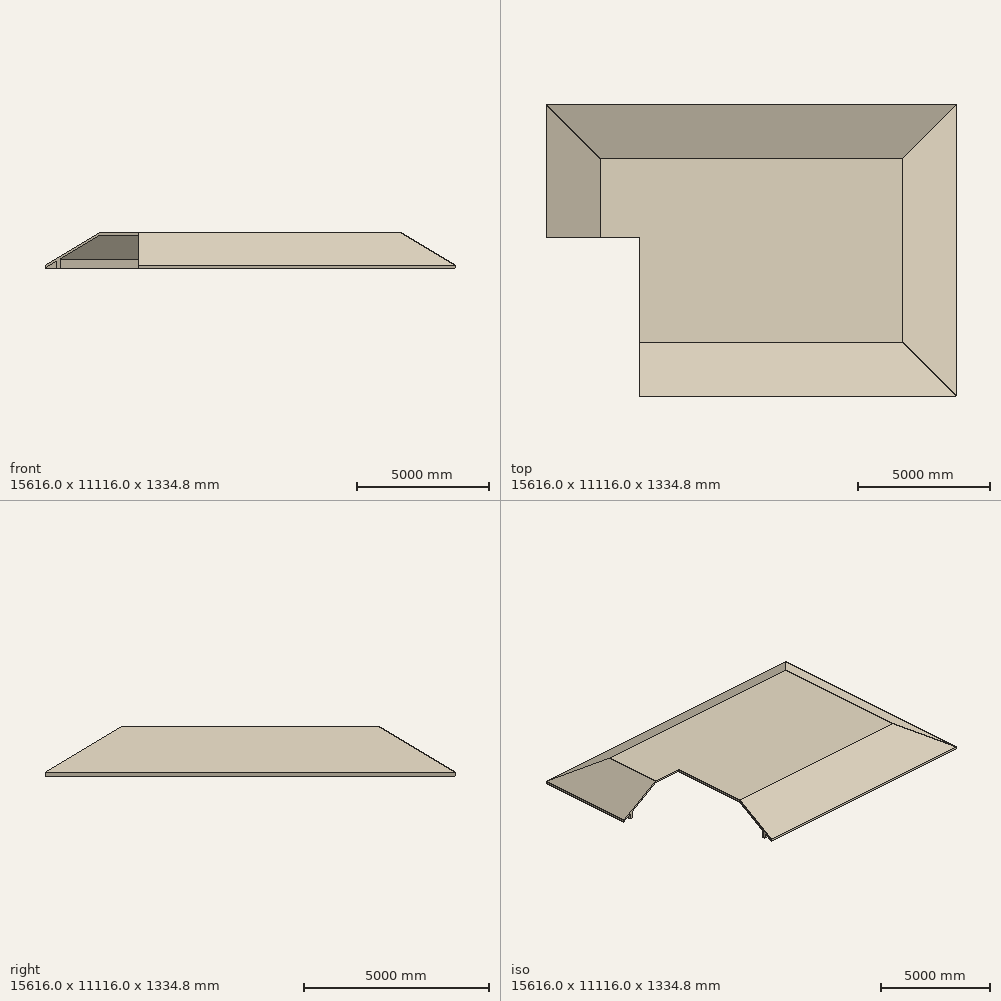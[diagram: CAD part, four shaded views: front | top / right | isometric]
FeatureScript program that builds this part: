
annotation { "Feature Type Name" : "Feature", "Feature Type Description" : "" }
export const myFeature = defineFeature(function(context is Context, id is Id, definition is map)
    precondition{}
    {
        {
            var Q0;
            Q0=qCreatedBy(makeId("Front.planeOp"),FACE);
            var sketch = newSketch(context, id + "F0", { "sketchPlane" : qUnion([Q0])});
            skLineSegment(sketch, "E0", {"start": v(1341.6, 842.92) * mm, "end": v(-158.4, -57.08) * mm});
            skLineSegment(sketch, "E1", {"start": v(-158.4, -57.08) * mm, "end": v(-158.4, -57.08) * mm});
            skLineSegment(sketch, "E2", {"start": v(-716.39, -391.87) * mm, "end": v(-716.39, -291.87) * mm});
            skLineSegment(sketch, "E3", {"start": v(-716.39, -291.87) * mm, "end": v(1341.6, 942.92) * mm});
            skLineSegment(sketch, "E4", {"start": v(1341.6, 942.92) * mm, "end": v(1341.6, 842.92) * mm});
            skLineSegment(sketch, "E5.bottom", {"start": v(-158.4, -391.87) * mm, "end": v(-308.4, -391.87) * mm});
            skLineSegment(sketch, "E5.left", {"start": v(-158.4, -391.87) * mm, "end": v(-158.4, -57.08) * mm});
            skLineSegment(sketch, "E5.right", {"start": v(-308.4, -391.87) * mm, "end": v(-308.4, -147.08) * mm});
            skLineSegment(sketch, "E6.trimOffspring", {"start": v(-308.4, -147.08) * mm, "end": v(-716.39, -391.87) * mm});
            skSolve(sketch);
        }
        {
            var Q0;
            Q0 = qSketchRegion(id + "F0", true);
            var Q1;
            Q1 = qBodyType(qCreatedBy(id + "F0" ,EDGE), BodyType.WIRE);
            extrude(context, id + "F1", {"entities" : qUnion([Q0]), "surfaceEntities" : qUnion([Q1]), "oppositeDirection" : true, "depth" : 5058 * mm, "offsetDistance" : 25 * mm});
        }
        {
            var Q0;
            Q0=makeQuery(id+"F1.opExtrude","SWEPT_FACE",FACE,{"disambiguationData":[OSD([sQuery(id+"F0.wireOp",EDGE,"E2")])]});
            var sketch = newSketch(context, id + "F2", { "sketchPlane" : qUnion([Q0])});
            skLineSegment(sketch, "E7", {"start": v(-3000.02, 842.92) * mm, "end": v(-4500.02, -57.08) * mm});
            skLineSegment(sketch, "E8", {"start": v(-4500.02, -57.08) * mm, "end": v(-4500.02, -57.08) * mm});
            skLineSegment(sketch, "E9", {"start": v(-5058, -391.87) * mm, "end": v(-5058, -291.87) * mm});
            skLineSegment(sketch, "E10", {"start": v(-5058, -291.87) * mm, "end": v(-3000.02, 942.92) * mm});
            skLineSegment(sketch, "E11", {"start": v(-3000.02, 942.92) * mm, "end": v(-3000.02, 842.92) * mm});
            skLineSegment(sketch, "E12.bottom", {"start": v(-4500.02, -391.87) * mm, "end": v(-4650.02, -391.87) * mm});
            skLineSegment(sketch, "E12.left", {"start": v(-4500.02, -391.87) * mm, "end": v(-4500.02, -57.08) * mm});
            skLineSegment(sketch, "E12.right", {"start": v(-4650.02, -391.87) * mm, "end": v(-4650.02, -147.08) * mm});
            skLineSegment(sketch, "E13.trimOffspring", {"start": v(-4650.02, -147.08) * mm, "end": v(-5058, -391.87) * mm});
            skSolve(sketch);
        }
        {
            var Q0;
            Q0 = qSketchRegion(id + "F2", true);
            extrude(context, id + "F3", {"entities" : qUnion([Q0]), "operationType" : NewBodyOperationType.ADD, "oppositeDirection" : true, "depth" : 16000 * mm, "offsetDistance" : 25 * mm});
        }
        {
            var Q0;
            Q0=makeQuery(id+"F3.boolean.opBoolean","MERGE",FACE,{"derivedFrom":[makeQuery(id+"F1.opExtrude","SWEPT_FACE",FACE,{"disambiguationData":[OSD([sQuery(id+"F0.wireOp",EDGE,"E2")])]}),makeQuery(id+"F3.opExtrude","CAP_FACE",FACE,{"disambiguationData":[OSD([sQuery(id+"F2.wireOp",EDGE,"E7"),sQuery(id+"F2.wireOp",EDGE,"E9"),sQuery(id+"F2.wireOp",EDGE,"E10"),sQuery(id+"F2.wireOp",EDGE,"E11"),sQuery(id+"F2.wireOp",EDGE,"E12.bottom"),sQuery(id+"F2.wireOp",EDGE,"E12.left"),sQuery(id+"F2.wireOp",EDGE,"E12.right"),sQuery(id+"F2.wireOp",EDGE,"E13.trimOffspring")])],"isStart":true})]});
            var sketch = newSketch(context, id + "F4", { "sketchPlane" : qUnion([Q0])});
            skLineSegment(sketch, "E14", {"start": v(-3000.02, 942.92) * mm, "end": v(-5058, -291.87) * mm});
            skLineSegment(sketch, "E15", {"start": v(-5058, -291.87) * mm, "end": v(-5058, 942.92) * mm});
            skLineSegment(sketch, "E16", {"start": v(-5058, 942.92) * mm, "end": v(-3000.02, 942.92) * mm});
            skSolve(sketch);
        }
        {
            var Q0;
            Q0 = qSketchRegion(id + "F4", true);
            extrude(context, id + "F5", {"entities" : qUnion([Q0]), "operationType" : NewBodyOperationType.REMOVE, "endBound" : BoundingType.THROUGH_ALL, "oppositeDirection" : true, "depth" : 25 * mm, "offsetDistance" : 25 * mm});
        }
        {
            var Q0;
            {var subQ2=sQuery(id+"F2.wireOp",EDGE,"E11");var subQ3=makeQuery(id+"F3.opExtrude","SWEPT_FACE",FACE,{"disambiguationData":[OSD([subQ2])]});Q0=makeQuery(id+"F3.boolean.opBoolean","SPLIT",FACE,{"disambiguationData":[TD([makeQuery(id+"F1.opExtrude","SWEPT_FACE",FACE,{"disambiguationData":[OSD([sQuery(id+"F0.wireOp",EDGE,"E2")])]})])],"derivedFrom":subQ3});}
            var sketch = newSketch(context, id + "F6", { "sketchPlane" : qUnion([Q0])});
            skLineSegment(sketch, "E17", {"start": v(1341.6, 942.92) * mm, "end": v(-716.39, 942.92) * mm});
            skLineSegment(sketch, "E18", {"start": v(-716.39, 942.92) * mm, "end": v(-716.39, -291.87) * mm});
            skLineSegment(sketch, "E19", {"start": v(-716.39, -291.87) * mm, "end": v(1341.6, 942.92) * mm});
            skSolve(sketch);
        }
        {
            var Q0;
            Q0 = qSketchRegion(id + "F6", true);
            extrude(context, id + "F7", {"entities" : qUnion([Q0]), "operationType" : NewBodyOperationType.REMOVE, "endBound" : BoundingType.THROUGH_ALL, "oppositeDirection" : true, "depth" : 25 * mm, "offsetDistance" : 25 * mm});
        }
        {
            var Q0;
            Q0=makeQuery(id+"F3.boolean.opBoolean","MERGE",FACE,{"derivedFrom":[makeQuery(id+"F1.opExtrude","CAP_FACE",FACE,{"disambiguationData":[OSD([sQuery(id+"F0.wireOp",EDGE,"E0"),sQuery(id+"F0.wireOp",EDGE,"E2"),sQuery(id+"F0.wireOp",EDGE,"E3"),sQuery(id+"F0.wireOp",EDGE,"E4"),sQuery(id+"F0.wireOp",EDGE,"E5.bottom"),sQuery(id+"F0.wireOp",EDGE,"E5.left"),sQuery(id+"F0.wireOp",EDGE,"E5.right"),sQuery(id+"F0.wireOp",EDGE,"E6.trimOffspring")])],"isStart":false}),makeQuery(id+"F3.opExtrude","SWEPT_FACE",FACE,{"disambiguationData":[OSD([sQuery(id+"F2.wireOp",EDGE,"E9")])]})]});
            var sketch = newSketch(context, id + "F8", { "sketchPlane" : qUnion([Q0])});
            skLineSegment(sketch, "E20", {"start": v(-12841.6, 842.92) * mm, "end": v(-14341.6, -57.08) * mm});
            skLineSegment(sketch, "E21", {"start": v(-14341.6, -57.08) * mm, "end": v(-14341.6, -57.08) * mm});
            skLineSegment(sketch, "E22", {"start": v(-14899.58, -391.87) * mm, "end": v(-14899.58, -291.87) * mm});
            skLineSegment(sketch, "E23", {"start": v(-14899.58, -291.87) * mm, "end": v(-12841.6, 942.92) * mm});
            skLineSegment(sketch, "E24", {"start": v(-12841.6, 942.92) * mm, "end": v(-12841.6, 842.92) * mm});
            skLineSegment(sketch, "E25.bottom", {"start": v(-14341.6, -391.87) * mm, "end": v(-14491.6, -391.87) * mm});
            skLineSegment(sketch, "E25.left", {"start": v(-14341.6, -391.87) * mm, "end": v(-14341.6, -57.08) * mm});
            skLineSegment(sketch, "E25.right", {"start": v(-14491.6, -391.87) * mm, "end": v(-14491.6, -147.08) * mm});
            skLineSegment(sketch, "E26.trimOffspring", {"start": v(-14491.6, -147.08) * mm, "end": v(-14899.58, -391.87) * mm});
            skSolve(sketch);
        }
        {
            var Q0;
            Q0 = qSketchRegion(id + "F8", true);
            extrude(context, id + "F9", {"entities" : qUnion([Q0]), "operationType" : NewBodyOperationType.ADD, "oppositeDirection" : true, "depth" : 12000 * mm, "offsetDistance" : 25 * mm});
        }
        {
            var Q0;
            Q0=makeQuery(id+"F9.boolean.opBoolean","MERGE",FACE,{"derivedFrom":[makeQuery(id+"F3.boolean.opBoolean","MERGE",FACE,{"derivedFrom":[makeQuery(id+"F1.opExtrude","CAP_FACE",FACE,{"disambiguationData":[OSD([sQuery(id+"F0.wireOp",EDGE,"E0"),sQuery(id+"F0.wireOp",EDGE,"E2"),sQuery(id+"F0.wireOp",EDGE,"E3"),sQuery(id+"F0.wireOp",EDGE,"E4"),sQuery(id+"F0.wireOp",EDGE,"E5.bottom"),sQuery(id+"F0.wireOp",EDGE,"E5.left"),sQuery(id+"F0.wireOp",EDGE,"E5.right"),sQuery(id+"F0.wireOp",EDGE,"E6.trimOffspring")])],"isStart":false}),makeQuery(id+"F3.opExtrude","SWEPT_FACE",FACE,{"disambiguationData":[OSD([sQuery(id+"F2.wireOp",EDGE,"E9")])]})]}),makeQuery(id+"F9.opExtrude","CAP_FACE",FACE,{"disambiguationData":[OSD([sQuery(id+"F8.wireOp",EDGE,"E20"),sQuery(id+"F8.wireOp",EDGE,"E22"),sQuery(id+"F8.wireOp",EDGE,"E23"),sQuery(id+"F8.wireOp",EDGE,"E24"),sQuery(id+"F8.wireOp",EDGE,"E25.bottom"),sQuery(id+"F8.wireOp",EDGE,"E25.left"),sQuery(id+"F8.wireOp",EDGE,"E25.right"),sQuery(id+"F8.wireOp",EDGE,"E26.trimOffspring")])],"isStart":true})]});
            var sketch = newSketch(context, id + "F10", { "sketchPlane" : qUnion([Q0])});
            skLineSegment(sketch, "E27", {"start": v(-12841.6, 942.92) * mm, "end": v(-14899.58, -291.87) * mm});
            skLineSegment(sketch, "E28", {"start": v(-14899.58, -291.87) * mm, "end": v(-14899.58, -391.87) * mm});
            skLineSegment(sketch, "E29", {"start": v(-14899.58, -391.87) * mm, "end": v(-15283.61, -391.87) * mm});
            skLineSegment(sketch, "E30", {"start": v(-15283.61, -391.87) * mm, "end": v(-15283.61, 942.92) * mm});
            skLineSegment(sketch, "E31", {"start": v(-15283.61, 942.92) * mm, "end": v(-12841.6, 942.92) * mm});
            skSolve(sketch);
        }
        {
            var Q0;
            Q0 = qSketchRegion(id + "F10", true);
            extrude(context, id + "F11", {"entities" : qUnion([Q0]), "operationType" : NewBodyOperationType.REMOVE, "endBound" : BoundingType.THROUGH_ALL, "oppositeDirection" : true, "depth" : 25 * mm, "offsetDistance" : 25 * mm});
        }
        {
            var Q0;
            {var subQ0=sQuery(id+"F8.wireOp",EDGE,"E24");var subQ3=makeQuery(id+"F9.opExtrude","SWEPT_FACE",FACE,{"disambiguationData":[OSD([subQ0])]});Q0=makeQuery(id+"F9.boolean.opBoolean","SPLIT",FACE,{"disambiguationData":[TD([makeQuery(id+"F3.opExtrude","SWEPT_FACE",FACE,{"disambiguationData":[OSD([sQuery(id+"F2.wireOp",EDGE,"E9")])]})])],"derivedFrom":subQ3});}
            var sketch = newSketch(context, id + "F12", { "sketchPlane" : qUnion([Q0])});
            skLineSegment(sketch, "E32", {"start": v(-3000.02, 942.92) * mm, "end": v(-5058, 942.92) * mm});
            skLineSegment(sketch, "E33", {"start": v(-5058, 942.92) * mm, "end": v(-5058, -291.87) * mm});
            skLineSegment(sketch, "E34", {"start": v(-5058, -291.87) * mm, "end": v(-3000.02, 942.92) * mm});
            skSolve(sketch);
        }
        {
            var Q0;
            Q0 = qSketchRegion(id + "F12", true);
            extrude(context, id + "F13", {"entities" : qUnion([Q0]), "operationType" : NewBodyOperationType.REMOVE, "endBound" : BoundingType.THROUGH_ALL, "oppositeDirection" : true, "depth" : 25 * mm, "offsetDistance" : 25 * mm});
        }
        {
            var Q0;
            {var subQ9=sQuery(id+"F8.wireOp",EDGE,"E22");var subQ14=makeQuery(id+"F9.opExtrude","SWEPT_FACE",FACE,{"disambiguationData":[OSD([subQ9])]});Q0=makeQuery(id+"F11.boolean.opBoolean","MERGE",FACE,{"derivedFrom":[makeQuery(id+"F9.boolean.opBoolean","SPLIT",FACE,{"disambiguationData":[TD([makeQuery(id+"F3.opExtrude","SWEPT_FACE",FACE,{"disambiguationData":[OSD([sQuery(id+"F2.wireOp",EDGE,"E12.left")])]})])],"derivedFrom":subQ14}),makeQuery(id+"F9.boolean.opBoolean","SPLIT",FACE,{"disambiguationData":[TD([makeQuery(id+"F3.opExtrude","SWEPT_FACE",FACE,{"disambiguationData":[OSD([sQuery(id+"F2.wireOp",EDGE,"E9")])]})])],"derivedFrom":subQ14}),makeQuery(id+"F11.opExtrude","SWEPT_FACE",FACE,{"disambiguationData":[OSD([sQuery(id+"F10.wireOp",EDGE,"E28")])]})]});}
            var sketch = newSketch(context, id + "F14", { "sketchPlane" : qUnion([Q0])});
            skLineSegment(sketch, "E35", {"start": v(-3999.98, 842.92) * mm, "end": v(-5499.98, -57.08) * mm});
            skLineSegment(sketch, "E36", {"start": v(-5499.98, -57.08) * mm, "end": v(-5499.98, -57.08) * mm});
            skLineSegment(sketch, "E37", {"start": v(-6057.97, -391.87) * mm, "end": v(-6057.97, -291.87) * mm});
            skLineSegment(sketch, "E38", {"start": v(-6057.97, -291.87) * mm, "end": v(-3999.98, 942.92) * mm});
            skLineSegment(sketch, "E39", {"start": v(-3999.98, 942.92) * mm, "end": v(-3999.98, 842.92) * mm});
            skLineSegment(sketch, "E40.bottom", {"start": v(-5499.98, -391.87) * mm, "end": v(-5649.98, -391.87) * mm});
            skLineSegment(sketch, "E40.left", {"start": v(-5499.98, -391.87) * mm, "end": v(-5499.98, -57.08) * mm});
            skLineSegment(sketch, "E40.right", {"start": v(-5649.98, -391.87) * mm, "end": v(-5649.98, -147.08) * mm});
            skLineSegment(sketch, "E41.trimOffspring", {"start": v(-5649.98, -147.08) * mm, "end": v(-6057.97, -391.87) * mm});
            skSolve(sketch);
        }
        {
            var Q0;
            Q0 = qSketchRegion(id + "F14", true);
            extrude(context, id + "F15", {"entities" : qUnion([Q0]), "operationType" : NewBodyOperationType.ADD, "oppositeDirection" : true, "depth" : 12058 * mm, "offsetDistance" : 25 * mm});
        }
        {
            var Q0;
            {var subQ9=sQuery(id+"F8.wireOp",EDGE,"E22");var subQ14=makeQuery(id+"F9.opExtrude","SWEPT_FACE",FACE,{"disambiguationData":[OSD([subQ9])]});Q0=makeQuery(id+"F15.boolean.opBoolean","MERGE",FACE,{"derivedFrom":[makeQuery(id+"F11.boolean.opBoolean","MERGE",FACE,{"derivedFrom":[makeQuery(id+"F9.boolean.opBoolean","SPLIT",FACE,{"disambiguationData":[TD([makeQuery(id+"F3.opExtrude","SWEPT_FACE",FACE,{"disambiguationData":[OSD([sQuery(id+"F2.wireOp",EDGE,"E12.left")])]})])],"derivedFrom":subQ14}),makeQuery(id+"F9.boolean.opBoolean","SPLIT",FACE,{"disambiguationData":[TD([makeQuery(id+"F3.opExtrude","SWEPT_FACE",FACE,{"disambiguationData":[OSD([sQuery(id+"F2.wireOp",EDGE,"E9")])]})])],"derivedFrom":subQ14}),makeQuery(id+"F11.opExtrude","SWEPT_FACE",FACE,{"disambiguationData":[OSD([sQuery(id+"F10.wireOp",EDGE,"E28")])]})]}),makeQuery(id+"F15.opExtrude","CAP_FACE",FACE,{"disambiguationData":[OSD([sQuery(id+"F14.wireOp",EDGE,"E35"),sQuery(id+"F14.wireOp",EDGE,"E37"),sQuery(id+"F14.wireOp",EDGE,"E38"),sQuery(id+"F14.wireOp",EDGE,"E39"),sQuery(id+"F14.wireOp",EDGE,"E40.bottom"),sQuery(id+"F14.wireOp",EDGE,"E40.left"),sQuery(id+"F14.wireOp",EDGE,"E40.right"),sQuery(id+"F14.wireOp",EDGE,"E41.trimOffspring")])],"isStart":true})]});}
            var sketch = newSketch(context, id + "F16", { "sketchPlane" : qUnion([Q0])});
            skLineSegment(sketch, "E42", {"start": v(-3999.98, 942.92) * mm, "end": v(-6057.97, -291.87) * mm});
            skLineSegment(sketch, "E43", {"start": v(-6057.97, -291.87) * mm, "end": v(-6057.97, -391.87) * mm});
            skLineSegment(sketch, "E44", {"start": v(-6057.97, -391.87) * mm, "end": v(-6942, -391.87) * mm});
            skLineSegment(sketch, "E45", {"start": v(-6942, -391.87) * mm, "end": v(-6942, 942.92) * mm});
            skLineSegment(sketch, "E46", {"start": v(-6942, 942.92) * mm, "end": v(-3999.98, 942.92) * mm});
            skSolve(sketch);
        }
        {
            var Q0;
            Q0 = qSketchRegion(id + "F16", true);
            extrude(context, id + "F17", {"entities" : qUnion([Q0]), "operationType" : NewBodyOperationType.REMOVE, "endBound" : BoundingType.THROUGH_ALL, "oppositeDirection" : true, "depth" : 25 * mm, "offsetDistance" : 25 * mm});
        }
        {
            var Q0;
            {var subQ0=sQuery(id+"F14.wireOp",EDGE,"E39");var subQ3=makeQuery(id+"F15.opExtrude","SWEPT_FACE",FACE,{"disambiguationData":[OSD([subQ0])]});Q0=makeQuery(id+"F15.boolean.opBoolean","SPLIT",FACE,{"disambiguationData":[TD([makeQuery(id+"F9.opExtrude","SWEPT_FACE",FACE,{"disambiguationData":[OSD([sQuery(id+"F8.wireOp",EDGE,"E22")])]})])],"derivedFrom":subQ3});}
            var sketch = newSketch(context, id + "F18", { "sketchPlane" : qUnion([Q0])});
            skLineSegment(sketch, "E47", {"start": v(-12841.6, 942.92) * mm, "end": v(-14899.58, 942.92) * mm});
            skLineSegment(sketch, "E48", {"start": v(-14899.58, 942.92) * mm, "end": v(-14899.58, -291.87) * mm});
            skLineSegment(sketch, "E49", {"start": v(-14899.58, -291.87) * mm, "end": v(-12841.6, 942.92) * mm});
            skSolve(sketch);
        }
        {
            var Q0;
            Q0 = qSketchRegion(id + "F18", true);
            extrude(context, id + "F19", {"entities" : qUnion([Q0]), "operationType" : NewBodyOperationType.REMOVE, "endBound" : BoundingType.THROUGH_ALL, "oppositeDirection" : true, "depth" : 25 * mm, "offsetDistance" : 25 * mm});
        }
        {
            var Q0;
            {var subQ1=sQuery(id+"F14.wireOp",EDGE,"E39");var subQ3=makeQuery(id+"F15.opExtrude","SWEPT_FACE",FACE,{"disambiguationData":[OSD([subQ1])]});Q0=makeQuery(id+"F15.boolean.opBoolean","SPLIT",FACE,{"disambiguationData":[TD([makeQuery(id+"F9.opExtrude","SWEPT_FACE",FACE,{"disambiguationData":[OSD([sQuery(id+"F8.wireOp",EDGE,"E20")])]})])],"derivedFrom":subQ3});}
            extrude(context, id + "F20", {"entities" : qUnion([Q0]), "operationType" : NewBodyOperationType.ADD, "endBound" : BoundingType.UP_TO_NEXT, "depth" : 25 * mm, "offsetDistance" : 25 * mm});
        }
        {
            var Q0;
            {var subQ1=sQuery(id+"F0.wireOp",EDGE,"E4");var subQ3=makeQuery(id+"F1.opExtrude","SWEPT_FACE",FACE,{"disambiguationData":[OSD([subQ1])]});Q0=makeQuery(id+"F3.boolean.opBoolean","SPLIT",FACE,{"disambiguationData":[TD([makeQuery(id+"F3.opExtrude","SWEPT_FACE",FACE,{"disambiguationData":[OSD([sQuery(id+"F2.wireOp",EDGE,"E7")])]})])],"derivedFrom":subQ3});}
            extrude(context, id + "F21", {"entities" : qUnion([Q0]), "operationType" : NewBodyOperationType.ADD, "endBound" : BoundingType.UP_TO_NEXT, "depth" : 25 * mm, "offsetDistance" : 25 * mm});
        }
    });
